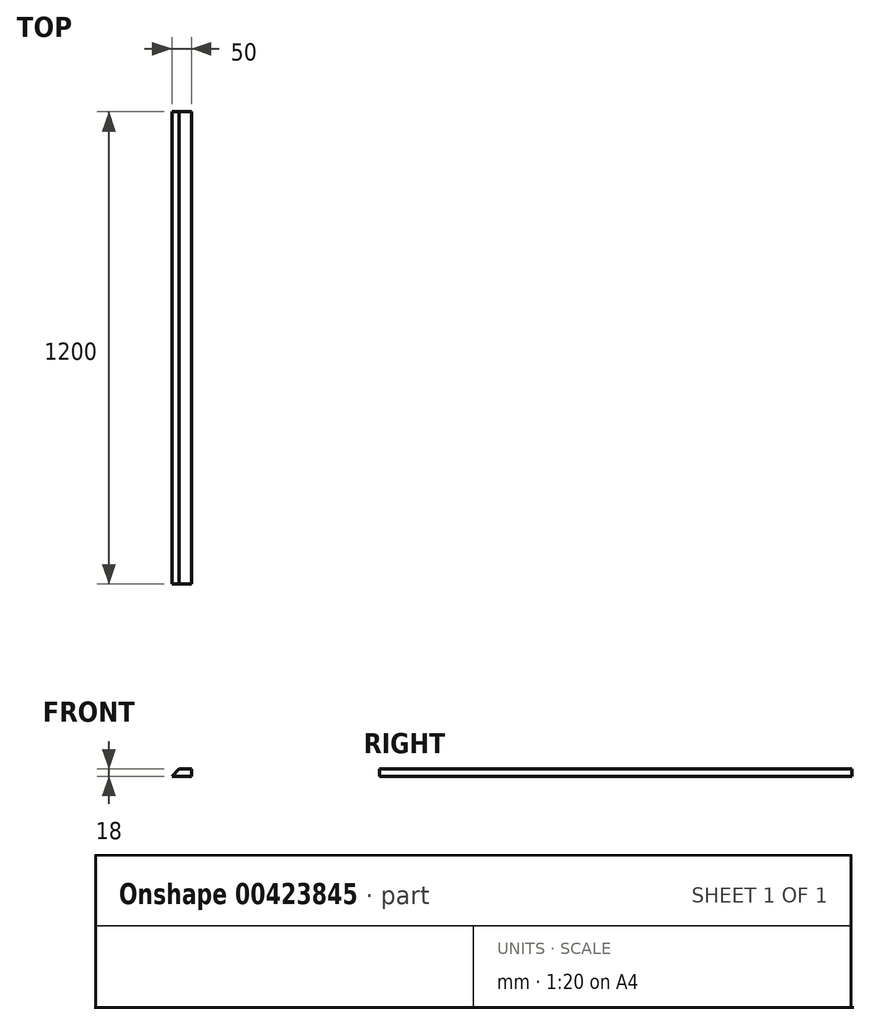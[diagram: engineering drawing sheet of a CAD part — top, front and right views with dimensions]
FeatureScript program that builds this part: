
annotation { "Feature Type Name" : "Feature", "Feature Type Description" : "" }
export const myFeature = defineFeature(function(context is Context, id is Id, definition is map)
    precondition{}
    {
        {
            var Q0;
            Q0=qCreatedBy(makeId("Front.planeOp"),FACE);
            var sketch = newSketch(context, id + "F0", { "sketchPlane" : qUnion([Q0])});
            skLineSegment(sketch, "E0", {"start": v(0, 0) * mm, "end": v(18, 18) * mm});
            skLineSegment(sketch, "E1", {"start": v(18, 18) * mm, "end": v(50, 18) * mm});
            skLineSegment(sketch, "E2", {"start": v(50, 18) * mm, "end": v(50, 0) * mm});
            skLineSegment(sketch, "E3", {"start": v(50, 0) * mm, "end": v(0, 0) * mm});
            skSolve(sketch);
        }
        {
            var Q0;
            Q0=qSketchRegion(id+"F0",true);
            extrude(context, id + "F1", {"entities" : qUnion([Q0]), "depth" : 1200 * mm});
        }
    });
